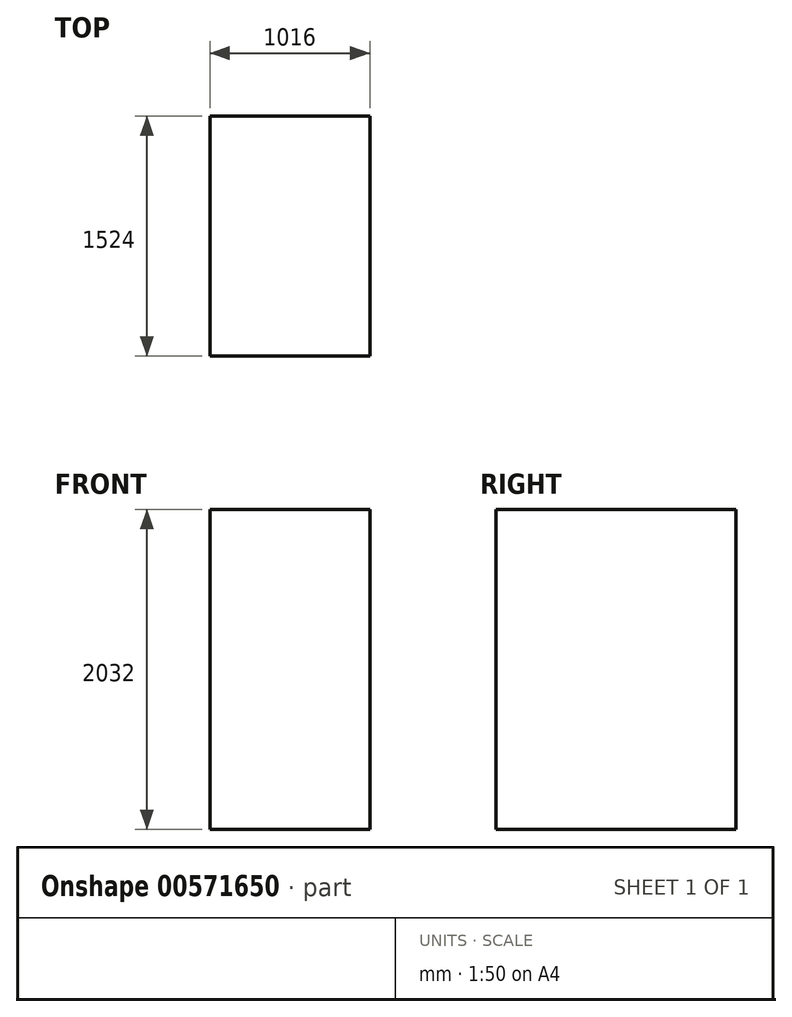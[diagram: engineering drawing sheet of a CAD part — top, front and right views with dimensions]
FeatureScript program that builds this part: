
annotation { "Feature Type Name" : "Feature", "Feature Type Description" : "" }
export const myFeature = defineFeature(function(context is Context, id is Id, definition is map)
    precondition{}
    {
        {
            var Q0;
            Q0=qCreatedBy(makeId("Top.planeOp"),FACE);
            var sketch = newSketch(context, id + "F0", { "sketchPlane" : qUnion([Q0])});
            skLineSegment(sketch, "E0.bottom", {"start": v(0, 0) * mm, "end": v(1016, 0) * mm});
            skLineSegment(sketch, "E0.top", {"start": v(0, 1524) * mm, "end": v(1016, 1524) * mm});
            skLineSegment(sketch, "E0.left", {"start": v(0, 0) * mm, "end": v(0, 1524) * mm});
            skLineSegment(sketch, "E0.right", {"start": v(1016, 0) * mm, "end": v(1016, 1524) * mm});
            skSolve(sketch);
        }
        {
            var Q0;
            Q0=makeQuery(id+"F0.imprint","IMPRINT",FACE,{"disambiguationData":[TD([[makeQuery(id+"F0.imprint","IMPRINT",EDGE,{"derivedFrom":sQuery(id+"F0.wireOp",EDGE,"E0.bottom")}),1.0]])]});
            extrude(context, id + "F1", {"entities" : qUnion([Q0]), "depth" : 2032 * mm, "offsetDistance" : 25.4 * mm});
        }
    });
